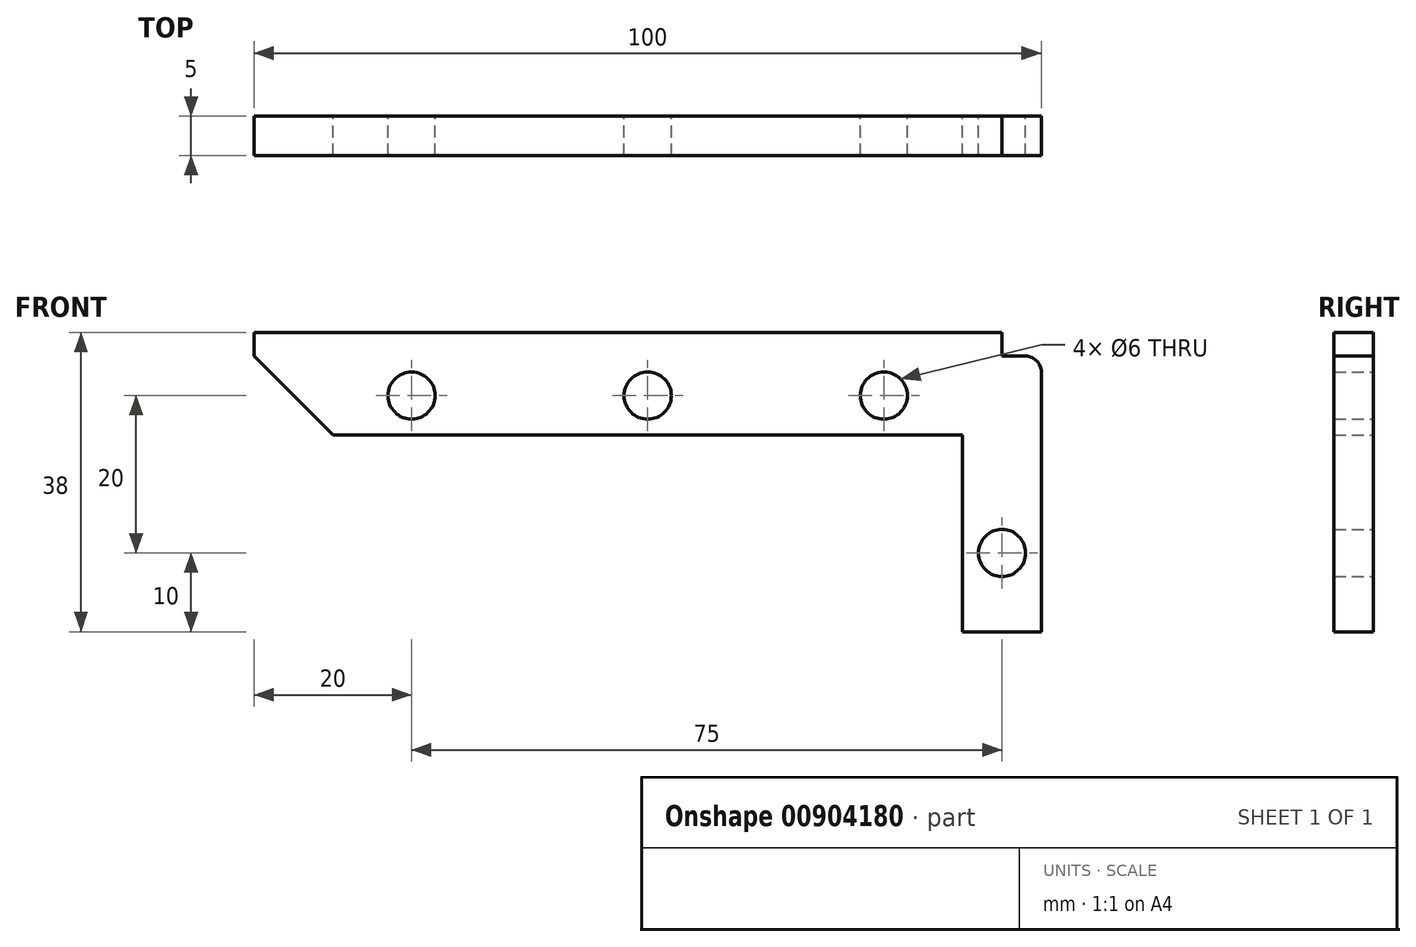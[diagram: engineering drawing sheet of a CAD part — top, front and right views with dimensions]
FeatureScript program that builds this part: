
annotation { "Feature Type Name" : "Feature", "Feature Type Description" : "" }
export const myFeature = defineFeature(function(context is Context, id is Id, definition is map)
    precondition{}
    {
        {
            var Q0;
            Q0=qCreatedBy(makeId("Front.planeOp"),FACE);
            var sketch = newSketch(context, id + "F0", { "sketchPlane" : qUnion([Q0])});
            skLineSegment(sketch, "E0.bottom", {"start": v(-50, 19) * mm, "end": v(45, 19) * mm});
            skLineSegment(sketch, "E0.top", {"start": v(40, -19) * mm, "end": v(50, -19) * mm});
            skLineSegment(sketch, "E0.left", {"start": v(-50, 19) * mm, "end": v(-50, 16) * mm});
            skLineSegment(sketch, "E0.right", {"start": v(50, 14) * mm, "end": v(50, -19) * mm});
            skPoint(sketch, "E0.middle", {"position": v(0, 0) * mm});
            skPoint(sketch, "E1", {"position": v(-40, -19) * mm});
            skPoint(sketch, "E2", {"position": v(-50, 16) * mm});
            skPoint(sketch, "E3", {"position": v(-40, 6) * mm});
            skPoint(sketch, "E4", {"position": v(-21.61, 28.03) * mm});
            skLineSegment(sketch, "E5", {"start": v(-50, 16) * mm, "end": v(-40, 6) * mm});
            skPoint(sketch, "E6", {"position": v(45, 19) * mm});
            skPoint(sketch, "E7", {"position": v(45, 16) * mm});
            skLineSegment(sketch, "E8", {"start": v(45, 19) * mm, "end": v(45, 16) * mm});
            skLineSegment(sketch, "E9", {"start": v(45, 16) * mm, "end": v(48, 16) * mm});
            skPoint(sketch, "E10", {"position": v(48, 14) * mm});
            skArc(sketch, "E11", {"start": v(50, 14) * mm, "mid": v(49.41, 15.41) * mm, "end": v(48, 16) * mm});
            skPoint(sketch, "E12", {"position": v(-30, 11) * mm});
            skPoint(sketch, "E13", {"position": v(0, 11) * mm});
            skPoint(sketch, "E14", {"position": v(30, 11) * mm});
            skPoint(sketch, "E15.orphan", {"position": v(-50, -19) * mm});
            skPoint(sketch, "E16.orphan", {"position": v(50, 19) * mm});
            skPoint(sketch, "E17.orphan", {"position": v(50, 16) * mm});
            skCircle(sketch, "E18", {"center": v(-30, 11) * mm, "radius": 3 * mm});
            skCircle(sketch, "E19", {"center": v(0, 11) * mm, "radius": 3 * mm});
            skCircle(sketch, "E20", {"center": v(30, 11) * mm, "radius": 3 * mm});
            skPoint(sketch, "E21", {"position": v(45, -9) * mm});
            skCircle(sketch, "E22", {"center": v(45, -9) * mm, "radius": 3 * mm});
            skLineSegment(sketch, "E23.bottom", {"start": v(-40, 6) * mm, "end": v(40, 6) * mm});
            skLineSegment(sketch, "E23.right", {"start": v(40, 6) * mm, "end": v(40, -19) * mm});
            skSolve(sketch);
        }
        {
            var Q0;
            Q0=makeQuery(id+"F0.imprint","IMPRINT",FACE,{"disambiguationData":[TD([[makeQuery(id+"F0.imprint","IMPRINT",EDGE,{"derivedFrom":sQuery(id+"F0.wireOp",EDGE,"E0.bottom")}),-1.0]])]});
            extrude(context, id + "F1", {"entities" : qUnion([Q0]), "depth" : 5 * mm, "offsetDistance" : 25 * mm});
        }
    });
